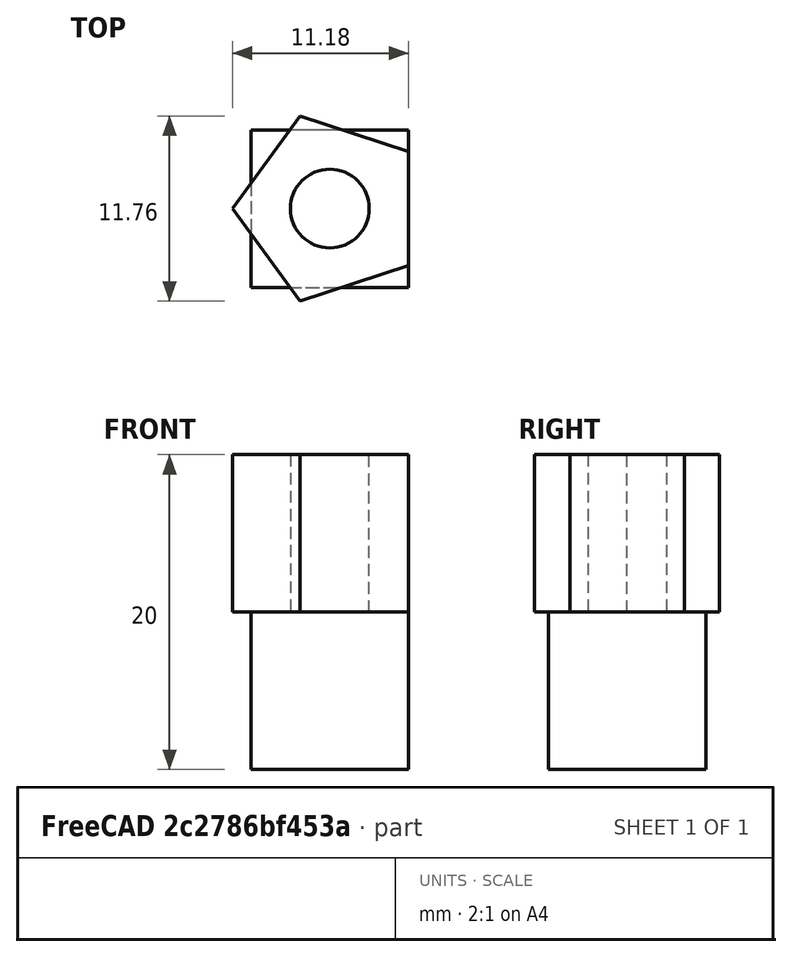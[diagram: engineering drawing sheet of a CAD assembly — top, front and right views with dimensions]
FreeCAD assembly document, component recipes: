
FREECAD ASSEMBLY — COMPONENT RECIPES ("xchg-components-c")

This assembly document has 4 components, labeled P0..P3 below (a component is one placed body or linked part). 4 of them carry a construction recipe — the FreeCAD feature program that regenerates the part from scratch, quoted from this document or its linked companion documents; the rest are supplied as boundary geometry only. No exploded tour is included for this assembly.
COMPONENT P0 — recipe-attached ("Cube 000", modeled in this document).
Construction recipe (the document's own serialized feature program — sketch geometry with constraints, then the solid features built on it; lengths are millimeters unless a unit is written):

FEATURE [Sketcher::SketchObject] Sketch001
  MapMode = 5
  Support = -> [XY_Plane001]
  sketch-geometry (5):
    g0: LineSegment StartX=5 StartY=5 StartZ=0 EndX=-5 EndY=5 EndZ=0
    g1: LineSegment StartX=-5 StartY=5 StartZ=0 EndX=-5 EndY=-5 EndZ=0
    g2: LineSegment StartX=-5 StartY=-5 StartZ=0 EndX=5 EndY=-5 EndZ=0
    g3: LineSegment StartX=5 StartY=-5 StartZ=0 EndX=5 EndY=5 EndZ=0
    g4: Circle [constr] CenterX=0 CenterY=0 CenterZ=0 NormalX=0 NormalY=0 NormalZ=1 AngleXU=0 Radius=7.07107
  constraints (14):
    c: Coincident(g0,g1)
    c: Coincident(g1,g2)
    c: Coincident(g2,g3)
    c: Coincident(g3,g0)
    c: Equal(g0,g1)
    c: Equal(g0,g2)
    c: Equal(g0,g3)
    c: PointOnObject(g0,g4)
    c: PointOnObject(g1,g4)
    c: PointOnObject(g2,g4)
    c: PointOnObject(g3,g4)
    c: Coincident(g4,g-1)
    c: Horizontal(g0)
    c: Distance(g2) = 10
FEATURE [PartDesign::Pad] Pad001
  ClaimChildren = false
  Length = 10
  Length2 = 100
  Profile = -> Sketch001
  Type = 0
FEATURE [PartDesign::Body] Body001  label="Cube 000"
  Group = -> [Sketch001,Pad001]
  Origin = -> Origin001
  Placement = pos=(0,0,-10) rot=(0,0,1;0rad)
  Tip = -> Pad001
COMPONENT P1 — recipe-attached ("Pentagon 000", modeled in this document).
Construction recipe (the document's own serialized feature program — sketch geometry with constraints, then the solid features built on it; lengths are millimeters unless a unit is written):

FEATURE [Sketcher::SketchObject] Sketch002
  MapMode = 5
  Support = -> [XY_Plane002]
  sketch-geometry (6):
    g0: LineSegment StartX=-6.18034 StartY=0 StartZ=0 EndX=-1.90983 EndY=-5.87785 EndZ=0
    g1: LineSegment StartX=-1.90983 StartY=-5.87785 StartZ=0 EndX=5 EndY=-3.63271 EndZ=0
    g2: LineSegment StartX=5 StartY=-3.63271 StartZ=0 EndX=5 EndY=3.63271 EndZ=0
    g3: LineSegment StartX=5 StartY=3.63271 StartZ=0 EndX=-1.90983 EndY=5.87785 EndZ=0
    g4: LineSegment StartX=-1.90983 StartY=5.87785 StartZ=0 EndX=-6.18034 EndY=0 EndZ=0
    g5: Circle [constr] CenterX=0 CenterY=0 CenterZ=0 NormalX=0 NormalY=0 NormalZ=1 AngleXU=0 Radius=6.18034
  constraints (14):
    c: Coincident(g0,g1)
    c: Coincident(g1,g2)
    c: Coincident(g2,g3)
    c: Coincident(g3,g4)
    c: Coincident(g4,g0)
    c: Equal(g0, g1-g4) x4
    c: PointOnObject(g0,g5)
    c: PointOnObject(g1,g5)
    c: PointOnObject(g2,g5)
    c: PointOnObject(g3,g5)
    c: PointOnObject(g4,g5)
    c: Coincident(g5,g-1)
    c: PointOnObject(g4,g-1)
    c: DistanceX(g-1,g1) = 5
FEATURE [PartDesign::Pad] Pad002
  ClaimChildren = false
  Length = 10
  Length2 = 100
  Profile = -> Sketch002
  Type = 0
FEATURE [PartDesign::Body] Body002  label="Pentagon 000"
  Group = -> [Sketch002,Pad002]
  Origin = -> Origin002
  Tip = -> Pad002
COMPONENT P2 — recipe-attached ("Cylinder 001", modeled in this document).
Construction recipe (the document's own serialized feature program — sketch geometry with constraints, then the solid features built on it; lengths are millimeters unless a unit is written):

FEATURE [Sketcher::SketchObject] Sketch
  MapMode = 5
  Support = -> [XY_Plane]
  sketch-geometry (1):
    g0: Circle CenterX=0 CenterY=0 CenterZ=0 NormalX=0 NormalY=0 NormalZ=1 AngleXU=0 Radius=2.5
  constraints (2):
    c: Coincident(g0,g-1)
    c: Diameter(g0) = 5
FEATURE [PartDesign::Pad] Pad
  ClaimChildren = false
  Length = 10
  Length2 = 100
  Profile = -> Sketch
  Type = 0
FEATURE [PartDesign::Body] Body  label="Cylinder 000"
  Group = -> [Sketch,Pad]
  Origin = -> Origin
  Tip = -> Pad
COMPONENT P3 — same part as P2; its construction recipe is shown at P2.
PROVENANCE & LICENSES
A FreeCAD (.FCStd) document from a public repository crawl; recipes are the document's own serialized feature recipes (and, for linked parts, companion documents' recipes).
License: as declared in the source repository (recorded in the dataset sidecar).
